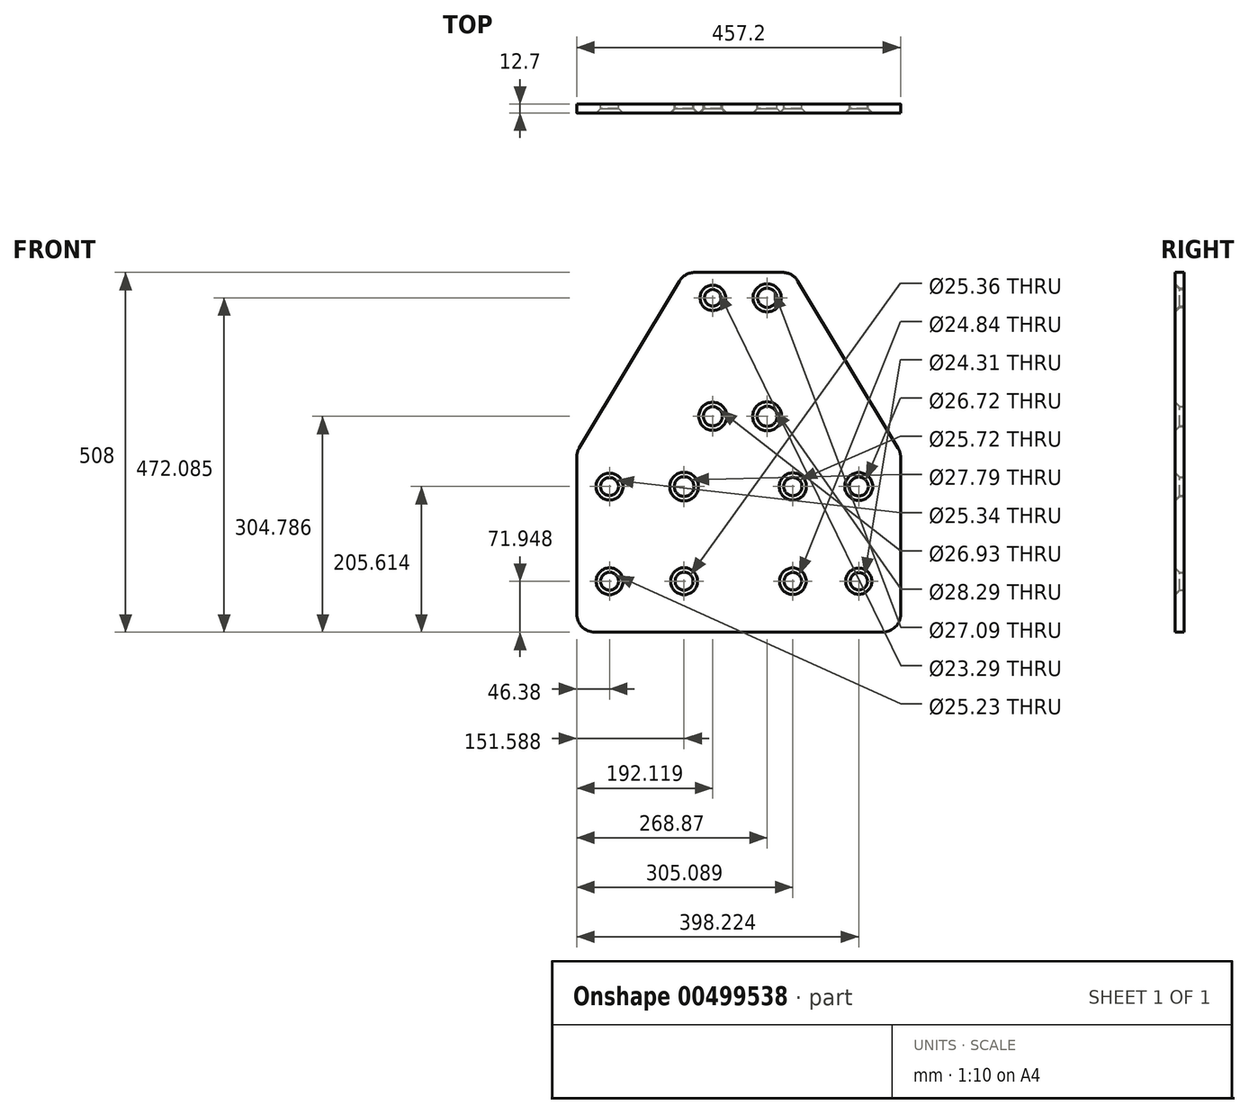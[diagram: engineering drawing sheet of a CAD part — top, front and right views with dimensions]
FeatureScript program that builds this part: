
annotation { "Feature Type Name" : "Feature", "Feature Type Description" : "" }
export const myFeature = defineFeature(function(context is Context, id is Id, definition is map)
    precondition{}
    {
        {
            var Q0;
            Q0=qCreatedBy(makeId("Front.planeOp"),FACE);
            var sketch = newSketch(context, id + "F0", { "sketchPlane" : qUnion([Q0])});
            skLineSegment(sketch, "E0.bottom", {"start": v(228.6, -152.09) * mm, "end": v(-228.6, -152.09) * mm});
            skLineSegment(sketch, "E0.left", {"start": v(228.6, -152.09) * mm, "end": v(228.6, 101.91) * mm});
            skLineSegment(sketch, "E0.right", {"start": v(-228.6, -152.09) * mm, "end": v(-228.6, 101.91) * mm});
            skLineSegment(sketch, "E1.top", {"start": v(76.2, 355.91) * mm, "end": v(-76.2, 355.91) * mm});
            skLineSegment(sketch, "E2", {"start": v(-76.2, 355.91) * mm, "end": v(-228.6, 101.91) * mm});
            skLineSegment(sketch, "E3", {"start": v(76.2, 355.91) * mm, "end": v(228.6, 101.91) * mm});
            skPoint(sketch, "E4", {"position": v(-36.48, 320) * mm});
            skPoint(sketch, "E5", {"position": v(40.27, 320) * mm});
            skPoint(sketch, "E6", {"position": v(40.27, 152.7) * mm});
            skPoint(sketch, "E7", {"position": v(-36.48, 152.7) * mm});
            skPoint(sketch, "E8", {"position": v(-182.22, 53.52) * mm});
            skPoint(sketch, "E9", {"position": v(-77.01, 53.52) * mm});
            skPoint(sketch, "E10", {"position": v(76.49, 53.52) * mm});
            skPoint(sketch, "E11", {"position": v(169.62, 53.52) * mm});
            skPoint(sketch, "E12", {"position": v(169.62, -80.14) * mm});
            skPoint(sketch, "E13", {"position": v(76.49, -80.14) * mm});
            skPoint(sketch, "E14", {"position": v(-77.01, -80.14) * mm});
            skPoint(sketch, "E15", {"position": v(-182.22, -80.14) * mm});
            skCircle(sketch, "E16", {"center": v(-36.48, 320) * mm, "radius": 11.64 * mm});
            skCircle(sketch, "E17", {"center": v(40.27, 320) * mm, "radius": 13.55 * mm});
            skCircle(sketch, "E18", {"center": v(40.27, 152.7) * mm, "radius": 14.14 * mm});
            skCircle(sketch, "E19", {"center": v(-36.48, 152.7) * mm, "radius": 13.46 * mm});
            skCircle(sketch, "E20", {"center": v(-182.22, 53.52) * mm, "radius": 12.67 * mm});
            skCircle(sketch, "E21", {"center": v(-77.01, 53.52) * mm, "radius": 13.9 * mm});
            skCircle(sketch, "E22", {"center": v(76.49, 53.52) * mm, "radius": 12.86 * mm});
            skCircle(sketch, "E23", {"center": v(169.62, 53.52) * mm, "radius": 13.36 * mm});
            skCircle(sketch, "E24", {"center": v(169.62, -80.14) * mm, "radius": 12.15 * mm});
            skCircle(sketch, "E25", {"center": v(76.49, -80.14) * mm, "radius": 12.42 * mm});
            skCircle(sketch, "E26", {"center": v(-77.01, -80.14) * mm, "radius": 12.68 * mm});
            skCircle(sketch, "E27", {"center": v(-182.22, -80.14) * mm, "radius": 12.62 * mm});
            skSolve(sketch);
        }
        {
            var Q0;
            Q0=makeQuery(id+"F0.imprint","IMPRINT",FACE,{"disambiguationData":[TD([[makeQuery(id+"F0.imprint","IMPRINT",EDGE,{"derivedFrom":sQuery(id+"F0.wireOp",EDGE,"E0.bottom")}),-1.0]])]});
            extrude(context, id + "F1", {"entities" : qUnion([Q0]), "depth" : 12.7 * mm, "offsetDistance" : 25.4 * mm});
        }
        {
            var Q0;
            Q0=makeQuery(id+"F1.opExtrude","SWEPT_EDGE",EDGE,{"disambiguationData":[OSD([sQuery(id+"F0.wireOp",EDGE,"E1.top"),sQuery(id+"F0.wireOp",EDGE,"E3")])]});
            var Q1;
            Q1=makeQuery(id+"F1.opExtrude","SWEPT_EDGE",EDGE,{"disambiguationData":[OSD([sQuery(id+"F0.wireOp",EDGE,"E1.top"),sQuery(id+"F0.wireOp",EDGE,"E2")])]});
            var Q2;
            Q2=makeQuery(id+"F1.opExtrude","SWEPT_EDGE",EDGE,{"disambiguationData":[OSD([sQuery(id+"F0.wireOp",EDGE,"E0.left"),sQuery(id+"F0.wireOp",EDGE,"E3")])]});
            var Q3;
            Q3=makeQuery(id+"F1.opExtrude","SWEPT_EDGE",EDGE,{"disambiguationData":[OSD([sQuery(id+"F0.wireOp",EDGE,"E0.bottom"),sQuery(id+"F0.wireOp",EDGE,"E0.left")])]});
            var Q4;
            Q4=makeQuery(id+"F1.opExtrude","SWEPT_EDGE",EDGE,{"disambiguationData":[OSD([sQuery(id+"F0.wireOp",EDGE,"E0.bottom"),sQuery(id+"F0.wireOp",EDGE,"E0.right")])]});
            var Q5;
            Q5=makeQuery(id+"F1.opExtrude","SWEPT_EDGE",EDGE,{"disambiguationData":[OSD([sQuery(id+"F0.wireOp",EDGE,"E0.right"),sQuery(id+"F0.wireOp",EDGE,"E2")])]});
            fillet(context, id + "F2", {"entities" : qUnion([Q0, Q1, Q2, Q3, Q4, Q5]), "radius" : 25.4 * mm, "tangentPropagation" : true, "allowEdgeOverflow" : false});
        }
        {
            var Q0;
            Q0=makeQuery(id+"F1.opExtrude","CAP_EDGE",EDGE,{"disambiguationData":[OSD([sQuery(id+"F0.wireOp",EDGE,"E17")])],"isStart":false});
            var Q1;
            Q1=makeQuery(id+"F1.opExtrude","CAP_EDGE",EDGE,{"disambiguationData":[OSD([sQuery(id+"F0.wireOp",EDGE,"E16")])],"isStart":false});
            var Q2;
            Q2=makeQuery(id+"F1.opExtrude","CAP_EDGE",EDGE,{"disambiguationData":[OSD([sQuery(id+"F0.wireOp",EDGE,"E19")])],"isStart":false});
            var Q3;
            Q3=makeQuery(id+"F1.opExtrude","CAP_EDGE",EDGE,{"disambiguationData":[OSD([sQuery(id+"F0.wireOp",EDGE,"E18")])],"isStart":false});
            var Q4;
            Q4=makeQuery(id+"F1.opExtrude","CAP_EDGE",EDGE,{"disambiguationData":[OSD([sQuery(id+"F0.wireOp",EDGE,"E21")])],"isStart":false});
            var Q5;
            Q5=makeQuery(id+"F1.opExtrude","CAP_EDGE",EDGE,{"disambiguationData":[OSD([sQuery(id+"F0.wireOp",EDGE,"E20")])],"isStart":false});
            var Q6;
            Q6=makeQuery(id+"F1.opExtrude","CAP_EDGE",EDGE,{"disambiguationData":[OSD([sQuery(id+"F0.wireOp",EDGE,"E22")])],"isStart":false});
            var Q7;
            Q7=makeQuery(id+"F1.opExtrude","CAP_EDGE",EDGE,{"disambiguationData":[OSD([sQuery(id+"F0.wireOp",EDGE,"E23")])],"isStart":false});
            var Q8;
            Q8=makeQuery(id+"F1.opExtrude","CAP_EDGE",EDGE,{"disambiguationData":[OSD([sQuery(id+"F0.wireOp",EDGE,"E24")])],"isStart":false});
            var Q9;
            Q9=makeQuery(id+"F1.opExtrude","CAP_EDGE",EDGE,{"disambiguationData":[OSD([sQuery(id+"F0.wireOp",EDGE,"E25")])],"isStart":false});
            var Q10;
            Q10=makeQuery(id+"F1.opExtrude","CAP_EDGE",EDGE,{"disambiguationData":[OSD([sQuery(id+"F0.wireOp",EDGE,"E26")])],"isStart":false});
            var Q11;
            Q11=makeQuery(id+"F1.opExtrude","CAP_EDGE",EDGE,{"disambiguationData":[OSD([sQuery(id+"F0.wireOp",EDGE,"E27")])],"isStart":false});
            chamfer(context, id + "F3", {"entities" : qUnion([Q0, Q1, Q2, Q3, Q4, Q5, Q6, Q7, Q8, Q9, Q10, Q11]), "width" : 6.35 * mm, "tangentPropagation" : true});
        }
    });
